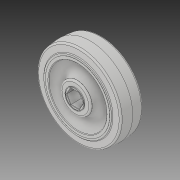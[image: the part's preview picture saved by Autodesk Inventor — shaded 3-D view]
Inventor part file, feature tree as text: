
AUTODESK INVENTOR PART (.ipt)
format: ipt  version: 2019 (Build 230136000, 136)  size: 284,672 bytes
history: native  units: in
note: dims shown in document units (in); Inventor stores cm internally (conversion verified against a paired STEP export)
features: revolve x1
ambient origin geometry x8: Origin, YZ Plane, XZ Plane, XY Plane, X Axis, Y Axis, Z Axis, Center Point
bodies: Solid1 (feature_tree)
feature tree (1):
  revolve  "Revolve1"  [1 undecoded]
note: 1 required parameter value undecoded (feature->parameter linkage not recoverable at this tier; creation-order binding heuristic only, values carry confidence <= 0.55)
